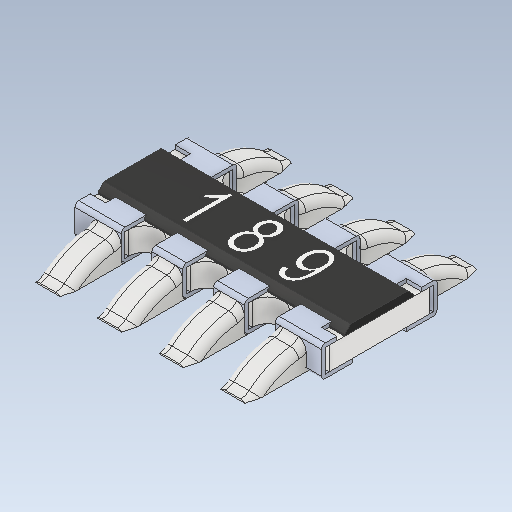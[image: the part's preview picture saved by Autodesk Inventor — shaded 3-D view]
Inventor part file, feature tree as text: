
AUTODESK INVENTOR PART (.ipt)
format: ipt  version: 2020.1 (Build 241239000, 239)  size: 596,992 bytes
history: native  units: mm
features: other x8, fillet x2
ambient origin geometry x8: Origin, YZ Plane, XZ Plane, XY Plane, X Axis, Y Axis, Z Axis, Center Point
bodies: Solid1 (feature_tree), Solid2 (feature_tree), Solid3 (feature_tree), Solid4 (feature_tree), Solid5 (feature_tree), Solid6 (feature_tree), Solid7 (feature_tree), Solid8 (feature_tree), Solid9 (feature_tree), Solid10 (feature_tree)
feature tree (10):
  other  "Cut-Extrude7"
  other  "Boss-Extrude5"
  fillet  "Fillet2"  [1 undecoded]
  fillet  "Fillet1"  [1 undecoded]
  other  "LPattern3[1]"
  other  "LPattern3[2]"
  other  "LPattern3[3]"
  other  "LPattern3[4]"
  other  "LPattern3[5]"
  other  "LPattern3[6]"
note: 2 required parameter values undecoded (feature->parameter linkage not recoverable at this tier; creation-order binding heuristic only, values carry confidence <= 0.55)
